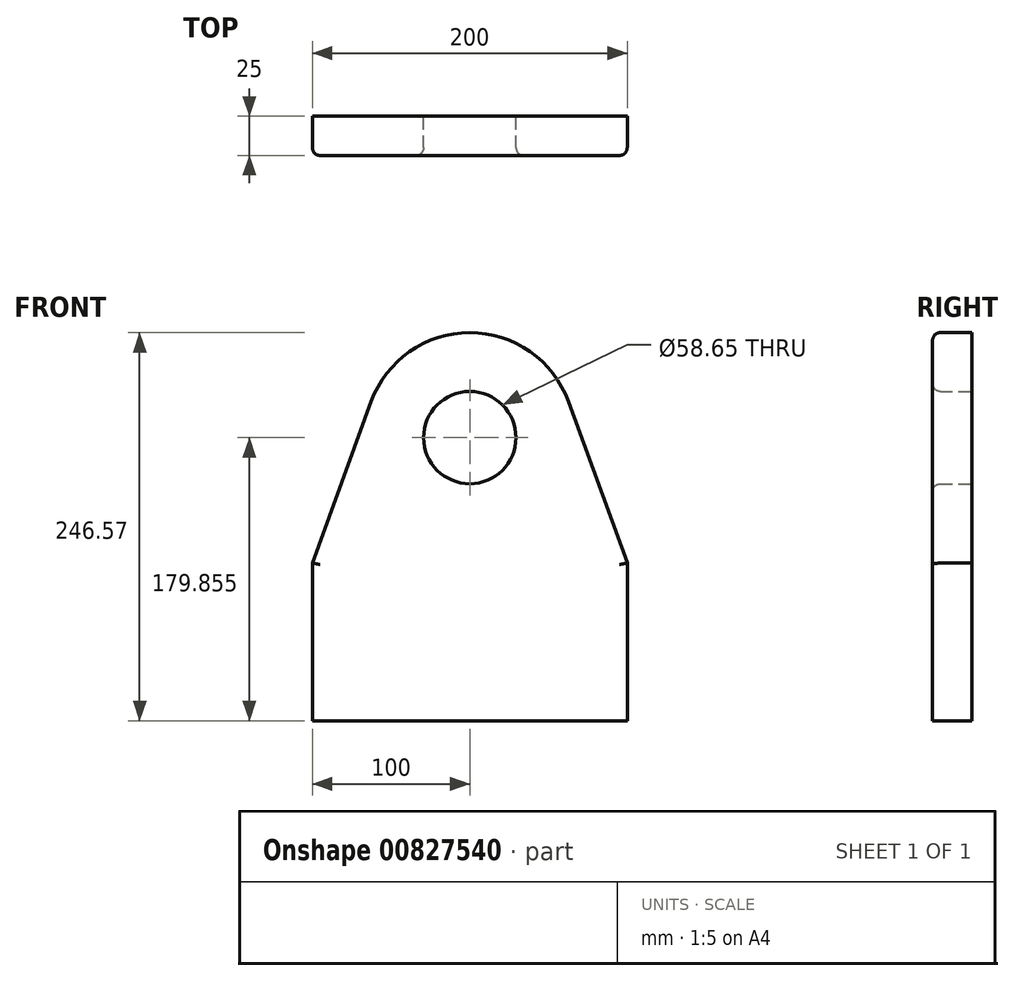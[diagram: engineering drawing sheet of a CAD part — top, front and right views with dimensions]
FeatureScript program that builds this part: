
annotation { "Feature Type Name" : "Feature", "Feature Type Description" : "" }
export const myFeature = defineFeature(function(context is Context, id is Id, definition is map)
    precondition{}
    {
        {
            var Q0;
            Q0=qCreatedBy(makeId("Front.planeOp"),FACE);
            var sketch = newSketch(context, id + "F0", { "sketchPlane" : qUnion([Q0])});
            skLineSegment(sketch, "E0.top", {"start": v(-100, -41.42) * mm, "end": v(100, -41.42) * mm});
            skLineSegment(sketch, "E0.left", {"start": v(-100, 58.74) * mm, "end": v(-100, -41.42) * mm});
            skLineSegment(sketch, "E0.right", {"start": v(100, 58.74) * mm, "end": v(100, -41.42) * mm});
            skCircle(sketch, "E1", {"center": v(0, 138.43) * mm, "radius": 29.33 * mm});
            skArc(sketch, "E2", {"start": v(62.7, 161.25) * mm, "mid": v(0, 205.15) * mm, "end": v(-62.7, 161.25) * mm});
            skLineSegment(sketch, "E3", {"start": v(-100, 58.74) * mm, "end": v(-62.7, 161.25) * mm});
            skLineSegment(sketch, "E4", {"start": v(100, 58.74) * mm, "end": v(62.7, 161.25) * mm});
            skSolve(sketch);
        }
        {
            var Q0;
            Q0 = qSketchRegion(id + "F0", true);
            extrude(context, id + "F1", {"entities" : qUnion([Q0]), "depth" : 25 * mm, "offsetDistance" : 25 * mm});
        }
        {
            var Q0;
            Q0=makeQuery(id+"F1.opExtrude","CAP_EDGE",EDGE,{"disambiguationData":[OSD([sQuery(id+"F0.wireOp",EDGE,"E1")])],"isStart":false});
            fillet(context, id + "F2", {"entities" : qUnion([Q0]), "radius" : 5 * mm, "tangentPropagation" : true, "allowEdgeOverflow" : false});
        }
        {
            var Q0;
            Q0=makeQuery(id+"F1.opExtrude","CAP_EDGE",EDGE,{"disambiguationData":[OSD([sQuery(id+"F0.wireOp",EDGE,"E0.left")])],"isStart":false});
            var Q1;
            Q1=makeQuery(id+"F1.opExtrude","CAP_EDGE",EDGE,{"disambiguationData":[OSD([sQuery(id+"F0.wireOp",EDGE,"E3")])],"isStart":false});
            var Q2;
            Q2=makeQuery(id+"F1.opExtrude","CAP_EDGE",EDGE,{"disambiguationData":[OSD([sQuery(id+"F0.wireOp",EDGE,"E2")])],"isStart":false});
            var Q3;
            Q3=makeQuery(id+"F1.opExtrude","CAP_EDGE",EDGE,{"disambiguationData":[OSD([sQuery(id+"F0.wireOp",EDGE,"E0.right")])],"isStart":false});
            var Q4;
            Q4=makeQuery(id+"F1.opExtrude","CAP_EDGE",EDGE,{"disambiguationData":[OSD([sQuery(id+"F0.wireOp",EDGE,"E4")])],"isStart":false});
            fillet(context, id + "F3", {"entities" : qUnion([Q0, Q1, Q2, Q3, Q4]), "radius" : 5 * mm, "tangentPropagation" : true, "allowEdgeOverflow" : false});
        }
    });
